# Revit family: Remeha_GasAce220-300_2Boilers-BackToBack_LOD3
name_source: partatom
category: Mechanical Equipment
revit_build: Autodesk Revit 2016 (Build: 20150714_1515(x64)
units: mm (PartAtom-declared; Revit-internal decimal feet)

## family parameters
Always vertical = Yes
Cut with Voids When Loaded = Yes
OmniClass Number = 23.75.10.11.14
OmniClass Title = Hot Water Heat Generators
Part Type = Normal
Room Calculation Point = No
Round Connector Dimension = Use Diameter
Shared = No
Work Plane-Based = No

## types (1)
- Gas Ace 220 - 2x300
    Access Clearance Bottom = 0.00 mm
    Access Clearance Front = 1100.00 mm
    Access Clearance Left = 500.00 mm
    Access Clearance Rear = 1100.00 mm
    Access Clearance Right = 500.00 mm
    Access Clearance Top = 0.00 mm
    Additional Technical Details = https://www.remeha.co.uk
    Air Inlet Connection Size = 200.00 mm
    BMS Links = Yes
    Building Regulations Seasonal Efficiency = 95.80
    Burner Control Type = Modulating
    CE Mark = 0063CQ3781
    Colour = RAL 2002 Red RAL7016 Dark Grey
    Condensate Drain Size = 40.00 mm
    Condensate Drain Type = Plain
    Configuration = Cascade boilers
    Control Type = 0 - 10V, Open Therm, Volt free enable, Direct boiler weather compensating control systems available from Remeha as optional extra's.
    Drain Connection Size = 20.00 mm
    Drain Connection Type = Unset
    Energy Technology List = https://etl.beis.gov.uk
    ErP Energy Label = 0
    ErP Rated Efficiency at Full Load = 87.7
    ErP Rated Efficiency at Part Load = 97.7
    ErP Seasonal Efficiency = 0
    Expected Life = 15
    External Material = Steel
    Features = Remeha's Gas 220 Ace  is a compact high efficiency floor standing condensing boiler. The compact design make this boiler ideally suited to modular arrangements
    Finish = High Polish Gardner 60 GRAD 91EH
    Flow and Return Connection Size = 125.00 mm
    Flow and Return Connection Type = Flanged
    Flue Connection size = 200.00 mm
    Flue or Air Intake Classification = B23P
    Frequency = 50 Hz
    Fuel Connection Size = 65.00 mm
    Fuel Connection Type = Flanged
    Full Load Current = 0 A
    Fuse Rating = 6 A
    Gas Consumption rate = 63.2
    Gross Weight = 1082.00 kg
    Heat Exchanger Material = Aluminium
    Heater Operation = Condensing
    Hydraulic Resistance at 11C temperature differential = 0.00000
    Hydraulic Resistance at 20C temperature differential = 0.20000
    IP Rating = IPX1B
    IfcExportAs = IfcBoilerType
    IfcExportType = NOTDEFINED
    Interlocks = Yes
    Load Classification = Power
    Manufacturer = Remeha Commercial
    Manufacturer Website = http://www.remeha.co.uk
    Maximum Gas Inlet Pressure = 0.02500 bar
    Maximum Oil Inlet Pressure = 0.00000 bar
    Maximum Operating Pressure = 5.00000 bar
    Maximum Power Consumption = 343 W
    Minimum Flow Rate at 11C temperature differential = 0.0 L/s
    Minimum Flow Rate at 20C temperature differential = 3.5 L/s
    Minimum Gas Inlet Pressure = 0.01700 bar
    Minimum Oil Inlet Pressure = 0.00000 bar
    Minimum Operating Pressure = 0.80000 bar
    Minimum Power Consumption = 9 W
    Monthly = 0
    Mounting = Floor Standing
    NOx Emissions = 35
    Nominal Gas Inlet Pressure = 0.02000 bar
    Nominal Oil Inlet Pressure = 0.00000 bar
    Oil Consumption rate = 0
    Operation and Maintenance Manual = https://www.remeha.co.uk
    Optional Fuel = Gas - LPG
    Overall Height = 2282.00 mm
    Overall Length = 2244.00 mm
    Overall Width = 1483.00 mm
    Primary Fuel = Gas - NG
    Product Literature = https://www.remeha.co.uk
    Product Model Number = KTSGA2B
    Product Range = Gas 220 -300 Back to Back Cascade 2 boilers in total
    Rated Criteria = 80/60
    Rated Output = 581800 W
    Reference Standard = GAD 2009/142/EC BED 92/42/EEC EMC 2014/30/EU LVD 2014/35/EU ErP 2009/125/EC
    Safety Valve Connection Size = 0.00 mm
    Safety Valve Connection Type = Unset
    Shape = Rectangular (Vertical)
    Shipping Weight = 0.00 kg
    Sound Pressure Level = 63.8
    Starting Current = 0 A
    Supply Phase = 1
    Turndown Ratio = 0
    Type = Space heating
    Voltage = 230 V
    Water Content = 193.0 L
    Water Treatment Required = Yes
    Weekly = 0

note: source unit labels omitted for Hydraulic Resistance at 11C temperature differential, Hydraulic Resistance at 20C temperature differential — the stored unit's dimension contradicts the parameter name (converter mislabeling)

## geometry (parser evidence)
native form markers: Sweep x17
no freeform markers — native parametric forms only
